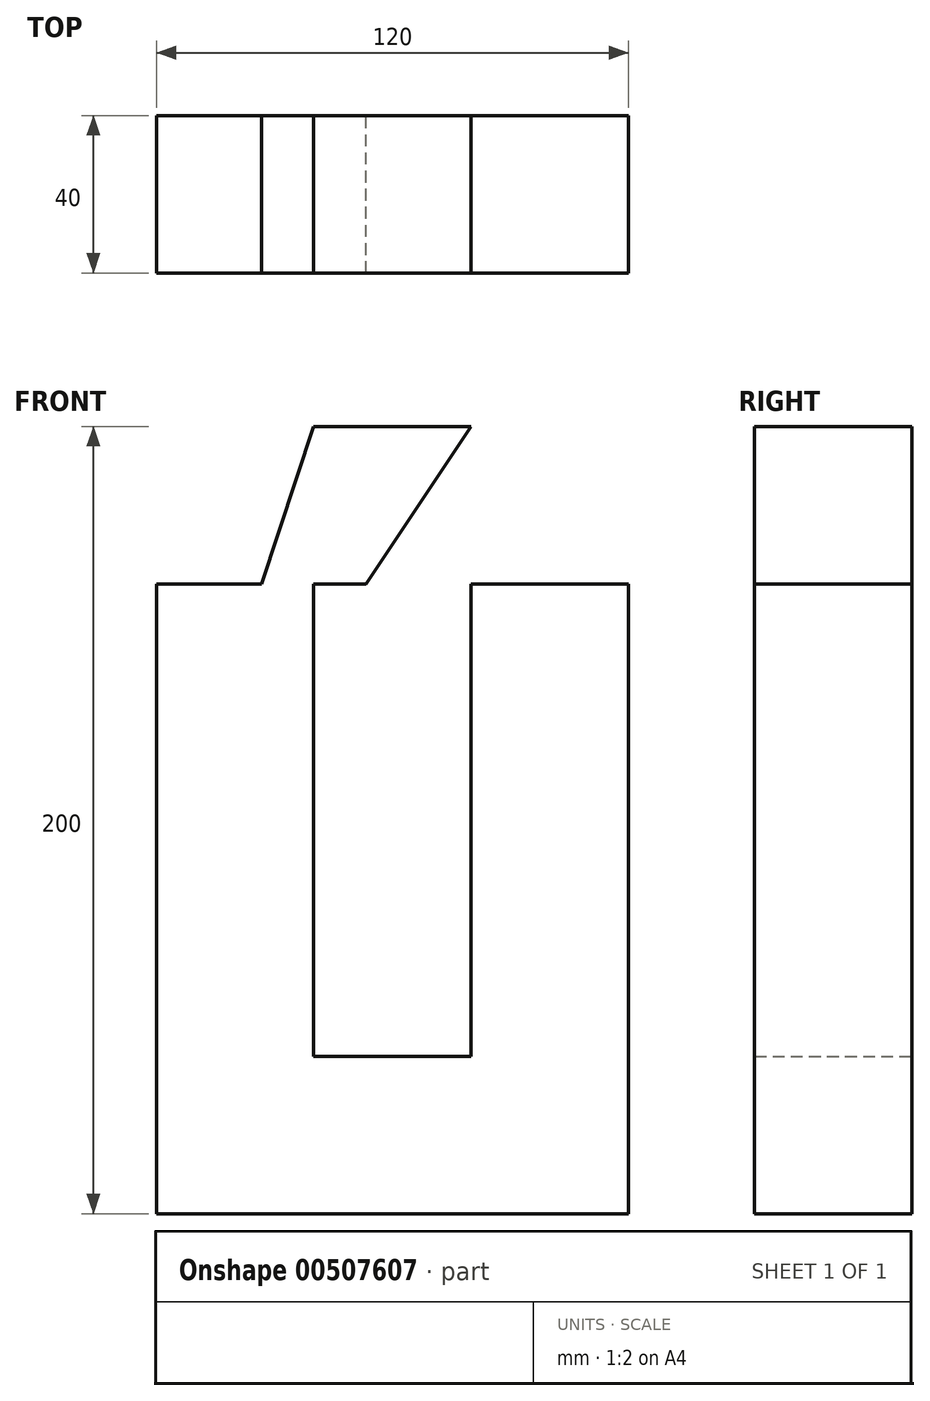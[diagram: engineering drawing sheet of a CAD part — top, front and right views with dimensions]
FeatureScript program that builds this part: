
annotation { "Feature Type Name" : "Feature", "Feature Type Description" : "" }
export const myFeature = defineFeature(function(context is Context, id is Id, definition is map)
    precondition{}
    {
        {
            var Q0;
            Q0=qCreatedBy(makeId("Front.planeOp"),FACE);
            var sketch = newSketch(context, id + "F0", { "sketchPlane" : qUnion([Q0])});
            skLineSegment(sketch, "E0.bottom", {"start": v(60, 100) * mm, "end": v(-60, 100) * mm});
            skLineSegment(sketch, "E0.top", {"start": v(60, -100) * mm, "end": v(-60, -100) * mm});
            skLineSegment(sketch, "E0.left", {"start": v(60, 100) * mm, "end": v(60, -100) * mm});
            skLineSegment(sketch, "E0.right", {"start": v(-60, 100) * mm, "end": v(-60, -100) * mm});
            skPoint(sketch, "E0.middle", {"position": v(0, 0) * mm});
            skLineSegment(sketch, "E1", {"start": v(-20, 100) * mm, "end": v(-20, -100) * mm});
            skLineSegment(sketch, "E2", {"start": v(20, 100) * mm, "end": v(20, -100) * mm});
            skLineSegment(sketch, "E3", {"start": v(60, 60) * mm, "end": v(-60, 60) * mm});
            skLineSegment(sketch, "E4", {"start": v(60, 20) * mm, "end": v(-60, 20) * mm});
            skLineSegment(sketch, "E5", {"start": v(60, -20) * mm, "end": v(-60, -20) * mm});
            skLineSegment(sketch, "E6", {"start": v(60, -60) * mm, "end": v(-60, -60) * mm});
            skLineSegment(sketch, "E7", {"start": v(-33.33, 60) * mm, "end": v(-20, 100) * mm});
            skLineSegment(sketch, "E8", {"start": v(-6.67, 60) * mm, "end": v(20, 100) * mm});
            skSolve(sketch);
        }
        {
            var Q0;
            {var subQ3=sQuery(id+"F0.wireOp",EDGE,"E8");Q0=makeQuery(id+"F0.imprint","IMPRINT",FACE,{"disambiguationData":[TD([[makeQuery(id+"F0.imprint","IMPRINT",EDGE,{"derivedFrom":subQ3}),1.0]])]});}
            var Q1;
            {var subQ0=sQuery(id+"F0.wireOp",EDGE,"E7");Q1=makeQuery(id+"F0.imprint","IMPRINT",FACE,{"disambiguationData":[TD([[makeQuery(id+"F0.imprint","IMPRINT",EDGE,{"derivedFrom":subQ0}),-1.0]])]});}
            var Q2;
            {var subQ0=sQuery(id+"F0.wireOp",EDGE,"E3");var subQ1=sQuery(id+"F0.wireOp",EDGE,"E0.right");var subQ2=makeQuery(id+"F0.imprint","INTERSECT",VERTEX,{"derivedFrom":[subQ1,subQ0]});Q2=makeQuery(id+"F0.imprint","IMPRINT",FACE,{"disambiguationData":[TD([[makeQuery(id+"F0.imprint","IMPRINT",EDGE,{"disambiguationData":[TD([[subQ2,-1.0]])],"derivedFrom":subQ1}),1.0]])]});}
            var Q3;
            {var subQ0=sQuery(id+"F0.wireOp",EDGE,"E4");var subQ1=sQuery(id+"F0.wireOp",EDGE,"E0.right");var subQ2=makeQuery(id+"F0.imprint","INTERSECT",VERTEX,{"derivedFrom":[subQ1,subQ0]});Q3=makeQuery(id+"F0.imprint","IMPRINT",FACE,{"disambiguationData":[TD([[makeQuery(id+"F0.imprint","IMPRINT",EDGE,{"disambiguationData":[TD([[subQ2,-1.0]])],"derivedFrom":subQ1}),1.0]])]});}
            var Q4;
            {var subQ0=sQuery(id+"F0.wireOp",EDGE,"E5");var subQ1=sQuery(id+"F0.wireOp",EDGE,"E0.right");var subQ2=makeQuery(id+"F0.imprint","INTERSECT",VERTEX,{"derivedFrom":[subQ1,subQ0]});Q4=makeQuery(id+"F0.imprint","IMPRINT",FACE,{"disambiguationData":[TD([[makeQuery(id+"F0.imprint","IMPRINT",EDGE,{"disambiguationData":[TD([[subQ2,-1.0]])],"derivedFrom":subQ1}),1.0]])]});}
            var Q5;
            {var subQ0=sQuery(id+"F0.wireOp",EDGE,"E0.right");var subQ1=sQuery(id+"F0.wireOp",EDGE,"E0.top");var subQ2=makeQuery(id+"F0.imprint","INTERSECT",VERTEX,{"derivedFrom":[subQ1,subQ0]});Q5=makeQuery(id+"F0.imprint","IMPRINT",FACE,{"disambiguationData":[TD([[makeQuery(id+"F0.imprint","IMPRINT",EDGE,{"disambiguationData":[TD([[subQ2,1.0]])],"derivedFrom":subQ1}),-1.0]])]});}
            var Q6;
            {var subQ0=sQuery(id+"F0.wireOp",EDGE,"E1");var subQ1=sQuery(id+"F0.wireOp",EDGE,"E0.top");var subQ2=makeQuery(id+"F0.imprint","INTERSECT",VERTEX,{"derivedFrom":[subQ1,subQ0]});Q6=makeQuery(id+"F0.imprint","IMPRINT",FACE,{"disambiguationData":[TD([[makeQuery(id+"F0.imprint","IMPRINT",EDGE,{"disambiguationData":[TD([[subQ2,1.0]])],"derivedFrom":subQ1}),-1.0]])]});}
            var Q7;
            {var subQ0=sQuery(id+"F0.wireOp",EDGE,"E0.left");var subQ1=sQuery(id+"F0.wireOp",EDGE,"E0.top");var subQ2=makeQuery(id+"F0.imprint","INTERSECT",VERTEX,{"derivedFrom":[subQ1,subQ0]});Q7=makeQuery(id+"F0.imprint","IMPRINT",FACE,{"disambiguationData":[TD([[makeQuery(id+"F0.imprint","IMPRINT",EDGE,{"disambiguationData":[TD([[subQ2,-1.0]])],"derivedFrom":subQ1}),-1.0]])]});}
            var Q8;
            {var subQ0=sQuery(id+"F0.wireOp",EDGE,"E5");var subQ1=sQuery(id+"F0.wireOp",EDGE,"E0.left");var subQ2=makeQuery(id+"F0.imprint","INTERSECT",VERTEX,{"derivedFrom":[subQ1,subQ0]});Q8=makeQuery(id+"F0.imprint","IMPRINT",FACE,{"disambiguationData":[TD([[makeQuery(id+"F0.imprint","IMPRINT",EDGE,{"disambiguationData":[TD([[subQ2,-1.0]])],"derivedFrom":subQ1}),-1.0]])]});}
            var Q9;
            {var subQ0=sQuery(id+"F0.wireOp",EDGE,"E4");var subQ1=sQuery(id+"F0.wireOp",EDGE,"E0.left");var subQ2=makeQuery(id+"F0.imprint","INTERSECT",VERTEX,{"derivedFrom":[subQ1,subQ0]});Q9=makeQuery(id+"F0.imprint","IMPRINT",FACE,{"disambiguationData":[TD([[makeQuery(id+"F0.imprint","IMPRINT",EDGE,{"disambiguationData":[TD([[subQ2,-1.0]])],"derivedFrom":subQ1}),-1.0]])]});}
            var Q10;
            {var subQ0=sQuery(id+"F0.wireOp",EDGE,"E3");var subQ1=sQuery(id+"F0.wireOp",EDGE,"E0.left");var subQ2=makeQuery(id+"F0.imprint","INTERSECT",VERTEX,{"derivedFrom":[subQ1,subQ0]});Q10=makeQuery(id+"F0.imprint","IMPRINT",FACE,{"disambiguationData":[TD([[makeQuery(id+"F0.imprint","IMPRINT",EDGE,{"disambiguationData":[TD([[subQ2,-1.0]])],"derivedFrom":subQ1}),-1.0]])]});}
            extrude(context, id + "F1", {"entities" : qUnion([Q0, Q1, Q2, Q3, Q4, Q5, Q6, Q7, Q8, Q9, Q10]), "depth" : 40 * mm, "offsetDistance" : 25 * mm});
        }
    });
